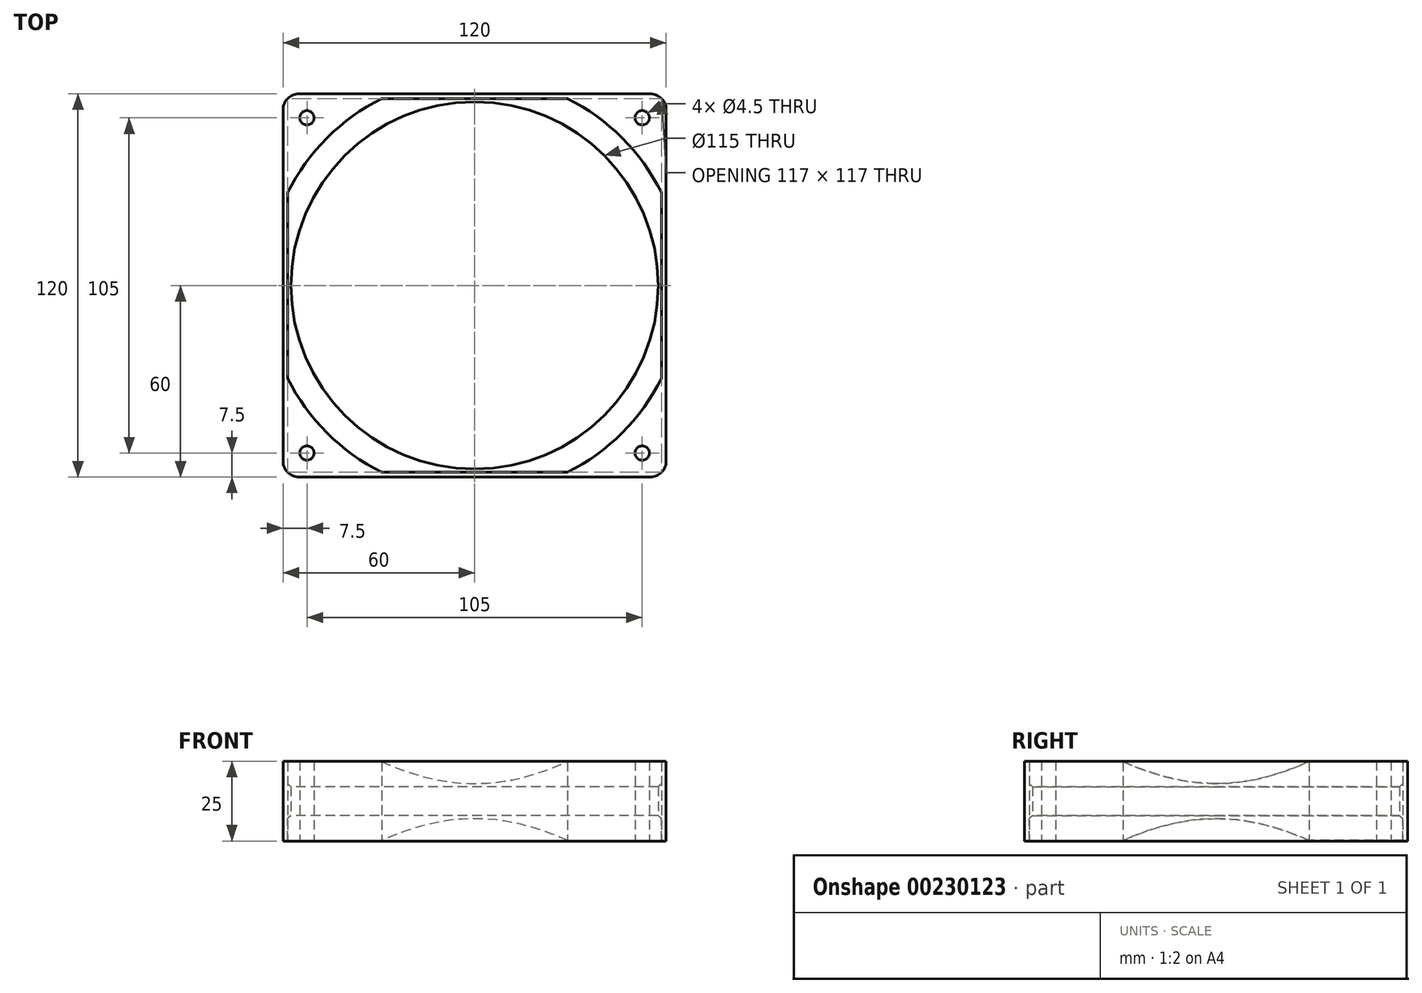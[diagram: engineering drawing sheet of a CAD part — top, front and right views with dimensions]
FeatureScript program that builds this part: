
annotation { "Feature Type Name" : "Feature", "Feature Type Description" : "" }
export const myFeature = defineFeature(function(context is Context, id is Id, definition is map)
    precondition{}
    {
        {
            var Q0;
            Q0=qCreatedBy(makeId("Top.planeOp"),FACE);
            var sketch = newSketch(context, id + "F0", { "sketchPlane" : qUnion([Q0])});
            skLineSegment(sketch, "E0.bottom", {"start": v(-55, 60) * mm, "end": v(55, 60) * mm});
            skLineSegment(sketch, "E0.top", {"start": v(-55, -60) * mm, "end": v(55, -60) * mm});
            skLineSegment(sketch, "E0.left", {"start": v(-60, 55) * mm, "end": v(-60, -55) * mm});
            skLineSegment(sketch, "E0.right", {"start": v(60, 55) * mm, "end": v(60, -55) * mm});
            skPoint(sketch, "E0.middle", {"position": v(0, 0) * mm});
            skLineSegment(sketch, "E1.bottom", {"start": v(-52.5, 52.5) * mm, "end": v(52.5, 52.5) * mm, "construction": true});
            skLineSegment(sketch, "E1.top", {"start": v(-52.5, -52.5) * mm, "end": v(52.5, -52.5) * mm, "construction": true});
            skLineSegment(sketch, "E1.left", {"start": v(-52.5, 52.5) * mm, "end": v(-52.5, -52.5) * mm, "construction": true});
            skLineSegment(sketch, "E1.right", {"start": v(52.5, 52.5) * mm, "end": v(52.5, -52.5) * mm, "construction": true});
            skCircle(sketch, "E2", {"center": v(-52.5, 52.5) * mm, "radius": 2.25 * mm});
            skCircle(sketch, "E3.0.1.0", {"center": v(-52.5, -52.5) * mm, "radius": 2.25 * mm});
            skCircle(sketch, "E3.1.0.0", {"center": v(52.5, 52.5) * mm, "radius": 2.25 * mm});
            skCircle(sketch, "E3.1.1.0", {"center": v(52.5, -52.5) * mm, "radius": 2.25 * mm});
            skPoint(sketch, "E4.visualSharp", {"position": v(-60, 60) * mm});
            skArc(sketch, "E4.filletArc", {"start": v(-55, 60) * mm, "mid": v(-58.54, 58.54) * mm, "end": v(-60, 55) * mm});
            skPoint(sketch, "E5.visualSharp", {"position": v(60, 60) * mm});
            skArc(sketch, "E5.filletArc", {"start": v(60, 55) * mm, "mid": v(58.54, 58.54) * mm, "end": v(55, 60) * mm});
            skPoint(sketch, "E6.visualSharp", {"position": v(60, -60) * mm});
            skArc(sketch, "E6.filletArc", {"start": v(55, -60) * mm, "mid": v(58.54, -58.54) * mm, "end": v(60, -55) * mm});
            skPoint(sketch, "E7.visualSharp", {"position": v(-60, -60) * mm});
            skArc(sketch, "E7.filletArc", {"start": v(-60, -55) * mm, "mid": v(-58.54, -58.54) * mm, "end": v(-55, -60) * mm});
            skCircle(sketch, "E8", {"center": v(0, 0) * mm, "radius": 57.5 * mm});
            skArc(sketch, "E9.0", {"start": v(-55, 58.5) * mm, "mid": v(-57.47, 57.47) * mm, "end": v(-58.5, 55) * mm});
            skLineSegment(sketch, "E9.1", {"start": v(-58.5, 55) * mm, "end": v(-58.5, 32.35) * mm});
            skLineSegment(sketch, "E9.2", {"start": v(-55, 58.5) * mm, "end": v(-32.35, 58.5) * mm});
            skArc(sketch, "E9.3", {"start": v(-58.5, -55) * mm, "mid": v(-57.47, -57.47) * mm, "end": v(-55, -58.5) * mm});
            skArc(sketch, "E9.4", {"start": v(58.5, 55) * mm, "mid": v(57.47, 57.47) * mm, "end": v(55, 58.5) * mm});
            skLineSegment(sketch, "E9.5", {"start": v(58.5, 55) * mm, "end": v(58.5, 32.35) * mm});
            skArc(sketch, "E9.6", {"start": v(55, -58.5) * mm, "mid": v(57.47, -57.47) * mm, "end": v(58.5, -55) * mm});
            skLineSegment(sketch, "E9.7", {"start": v(-55, -58.5) * mm, "end": v(-32.35, -58.5) * mm});
            skArc(sketch, "E10", {"start": v(-29.13, 58.5) * mm, "mid": v(-46.2, 46.2) * mm, "end": v(-58.5, 29.13) * mm});
            skArc(sketch, "E11.trimOffspring", {"start": v(-58.5, -29.13) * mm, "mid": v(-46.2, -46.2) * mm, "end": v(-29.13, -58.5) * mm});
            skArc(sketch, "E12.trimOffspring", {"start": v(29.13, -58.5) * mm, "mid": v(46.2, -46.2) * mm, "end": v(58.5, -29.13) * mm});
            skArc(sketch, "E13.trimOffspring", {"start": v(58.5, 29.13) * mm, "mid": v(46.2, 46.2) * mm, "end": v(29.13, 58.5) * mm});
            skArc(sketch, "E14.0", {"start": v(-58.5, -32.35) * mm, "mid": v(-47.27, -47.27) * mm, "end": v(-32.35, -58.5) * mm});
            skArc(sketch, "E15.0", {"start": v(32.35, -58.5) * mm, "mid": v(47.27, -47.27) * mm, "end": v(58.5, -32.35) * mm});
            skArc(sketch, "E16.0", {"start": v(58.5, 32.35) * mm, "mid": v(47.27, 47.27) * mm, "end": v(32.35, 58.5) * mm});
            skArc(sketch, "E17.0", {"start": v(-32.35, 58.5) * mm, "mid": v(-47.27, 47.27) * mm, "end": v(-58.5, 32.35) * mm});
            skLineSegment(sketch, "E18.trimOffspring", {"start": v(-58.5, -32.35) * mm, "end": v(-58.5, -55) * mm});
            skLineSegment(sketch, "E19.trimOffspring", {"start": v(-29.13, -58.5) * mm, "end": v(29.13, -58.5) * mm});
            skLineSegment(sketch, "E20.trimOffspring", {"start": v(32.35, -58.5) * mm, "end": v(55, -58.5) * mm});
            skLineSegment(sketch, "E21.trimOffspring", {"start": v(58.5, -32.35) * mm, "end": v(58.5, -55) * mm});
            skLineSegment(sketch, "E22.trimOffspring", {"start": v(58.5, 29.13) * mm, "end": v(58.5, -29.13) * mm});
            skLineSegment(sketch, "E23.trimOffspring", {"start": v(32.35, 58.5) * mm, "end": v(55, 58.5) * mm});
            skLineSegment(sketch, "E24.trimOffspring", {"start": v(-29.13, 58.5) * mm, "end": v(29.13, 58.5) * mm});
            skLineSegment(sketch, "E25.trimOffspring", {"start": v(-58.5, 29.13) * mm, "end": v(-58.5, -29.13) * mm});
            skSolve(sketch);
        }
        {
            var Q0;
            Q0 = qSketchRegion(id + "F0", true);
            var Q1;
            Q1=makeQuery(id+"F0.imprint","IMPRINT",FACE,{"disambiguationData":[TD([[makeQuery(id+"F0.imprint","IMPRINT",EDGE,{"derivedFrom":sQuery(id+"F0.wireOp",EDGE,"E2")}),-1.0]])]});
            var Q2;
            Q2=makeQuery(id+"F0.imprint","IMPRINT",FACE,{"disambiguationData":[TD([[makeQuery(id+"F0.imprint","IMPRINT",EDGE,{"derivedFrom":sQuery(id+"F0.wireOp",EDGE,"E3.1.0.0")}),-1.0]])]});
            var Q3;
            Q3=makeQuery(id+"F0.imprint","IMPRINT",FACE,{"disambiguationData":[TD([[makeQuery(id+"F0.imprint","IMPRINT",EDGE,{"derivedFrom":sQuery(id+"F0.wireOp",EDGE,"E3.1.1.0")}),-1.0]])]});
            var Q4;
            Q4=makeQuery(id+"F0.imprint","IMPRINT",FACE,{"disambiguationData":[TD([[makeQuery(id+"F0.imprint","IMPRINT",EDGE,{"derivedFrom":sQuery(id+"F0.wireOp",EDGE,"E3.0.1.0")}),-1.0]])]});
            extrude(context, id + "F1", {"entities" : qUnion([Q0, Q1, Q2, Q3, Q4]), "endBound" : BoundingType.SYMMETRIC, "depth" : 25 * mm});
        }
        {
            var Q0;
            Q0=makeQuery(id+"F0.imprint","IMPRINT",FACE,{"disambiguationData":[TD([[makeQuery(id+"F0.imprint","IMPRINT",EDGE,{"derivedFrom":sQuery(id+"F0.wireOp",EDGE,"E8")}),-1.0]])]});
            extrude(context, id + "F2", {"entities" : qUnion([Q0]), "endBound" : BoundingType.SYMMETRIC, "depth" : 25 * mm});
        }
        {
            var Q0;
            Q0=makeQuery(id+"F2.opExtrude","CAP_EDGE",EDGE,{"disambiguationData":[OSD([sQuery(id+"F0.wireOp",EDGE,"E8")])],"isStart":false});
            var Q1;
            Q1=makeQuery(id+"F2.opExtrude","CAP_EDGE",EDGE,{"disambiguationData":[OSD([sQuery(id+"F0.wireOp",EDGE,"E8")])],"isStart":true});
            chamfer(context, id + "F3", {"entities" : qUnion([Q0, Q1]), "width" : 8 * mm, "tangentPropagation" : true});
        }
    });
